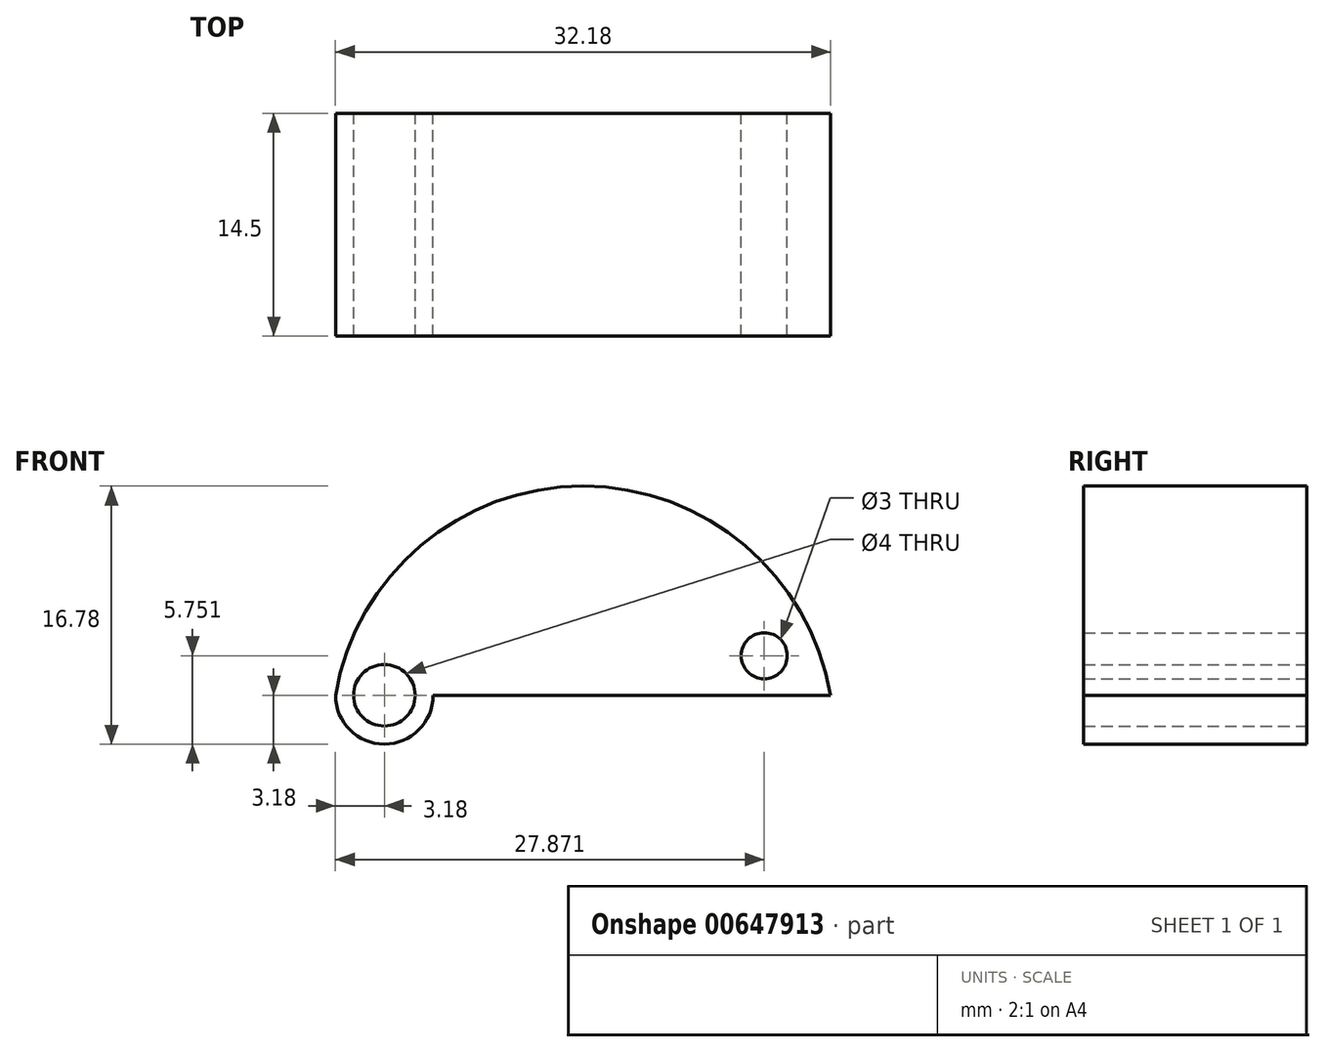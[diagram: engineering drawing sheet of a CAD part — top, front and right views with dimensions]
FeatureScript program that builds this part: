
annotation { "Feature Type Name" : "Feature", "Feature Type Description" : "" }
export const myFeature = defineFeature(function(context is Context, id is Id, definition is map)
    precondition{}
    {
        {
            var Q0;
            Q0=qCreatedBy(makeId("Front.planeOp"),FACE);
            var sketch = newSketch(context, id + "F0", { "sketchPlane" : qUnion([Q0])});
            skCircle(sketch, "E0", {"center": v(0, 0) * mm, "radius": 2 * mm});
            skCircle(sketch, "E1", {"center": v(0, 0) * mm, "radius": 3.18 * mm});
            skPoint(sketch, "E2", {"position": v(-3.18, 0) * mm});
            skPoint(sketch, "E3", {"position": v(29, 0) * mm});
            skCircle(sketch, "E4", {"center": v(12.91, -2.71) * mm, "radius": 16.31 * mm});
            skPoint(sketch, "E4.third.point", {"position": v(25.36, -13.26) * mm});
            skLineSegment(sketch, "E5", {"start": v(0, 0) * mm, "end": v(29, 0) * mm});
            skPoint(sketch, "E6", {"position": v(24.7, 2.57) * mm});
            skCircle(sketch, "E7", {"center": v(24.7, 2.57) * mm, "radius": 1.5 * mm});
            skSolve(sketch);
        }
        {
            var Q0;
            {var subQ0=sQuery(id+"F0.wireOp",EDGE,"E4");var subQ1=sQuery(id+"F0.wireOp",EDGE,"E1");var subQ2=makeQuery(id+"F0.imprint","INTERSECT",VERTEX,{"disambiguationData":[OD(0.0)],"derivedFrom":[subQ1,subQ0]});Q0=makeQuery(id+"F0.imprint","IMPRINT",FACE,{"disambiguationData":[TD([[makeQuery(id+"F0.imprint","IMPRINT",EDGE,{"disambiguationData":[TD([[subQ2,1.0]])],"derivedFrom":subQ1}),-1.0]])]});}
            extrude(context, id + "F1", {"entities" : qUnion([Q0]), "depth" : 14.5 * mm, "offsetDistance" : 25.4 * mm});
        }
        {
            var Q0;
            {var subQ0=sQuery(id+"F0.wireOp",EDGE,"E4");var subQ1=sQuery(id+"F0.wireOp",EDGE,"E1");var subQ2=makeQuery(id+"F0.imprint","INTERSECT",VERTEX,{"disambiguationData":[OD(0.0)],"derivedFrom":[subQ1,subQ0]});Q0=makeQuery(id+"F0.imprint","IMPRINT",FACE,{"disambiguationData":[TD([[makeQuery(id+"F0.imprint","IMPRINT",EDGE,{"disambiguationData":[TD([[subQ2,1.0]])],"derivedFrom":subQ1}),-1.0]])]});}
            var Q1;
            Q1=makeQuery(id+"F0.imprint","IMPRINT",FACE,{"disambiguationData":[TD([[makeQuery(id+"F0.imprint","IMPRINT",EDGE,{"derivedFrom":sQuery(id+"F0.wireOp",EDGE,"E0")}),-1.0]])]});
            extrude(context, id + "F2", {"entities" : qUnion([Q0, Q1]), "operationType" : NewBodyOperationType.ADD, "depth" : 14.5 * mm, "offsetDistance" : 25 * mm});
        }
    });
